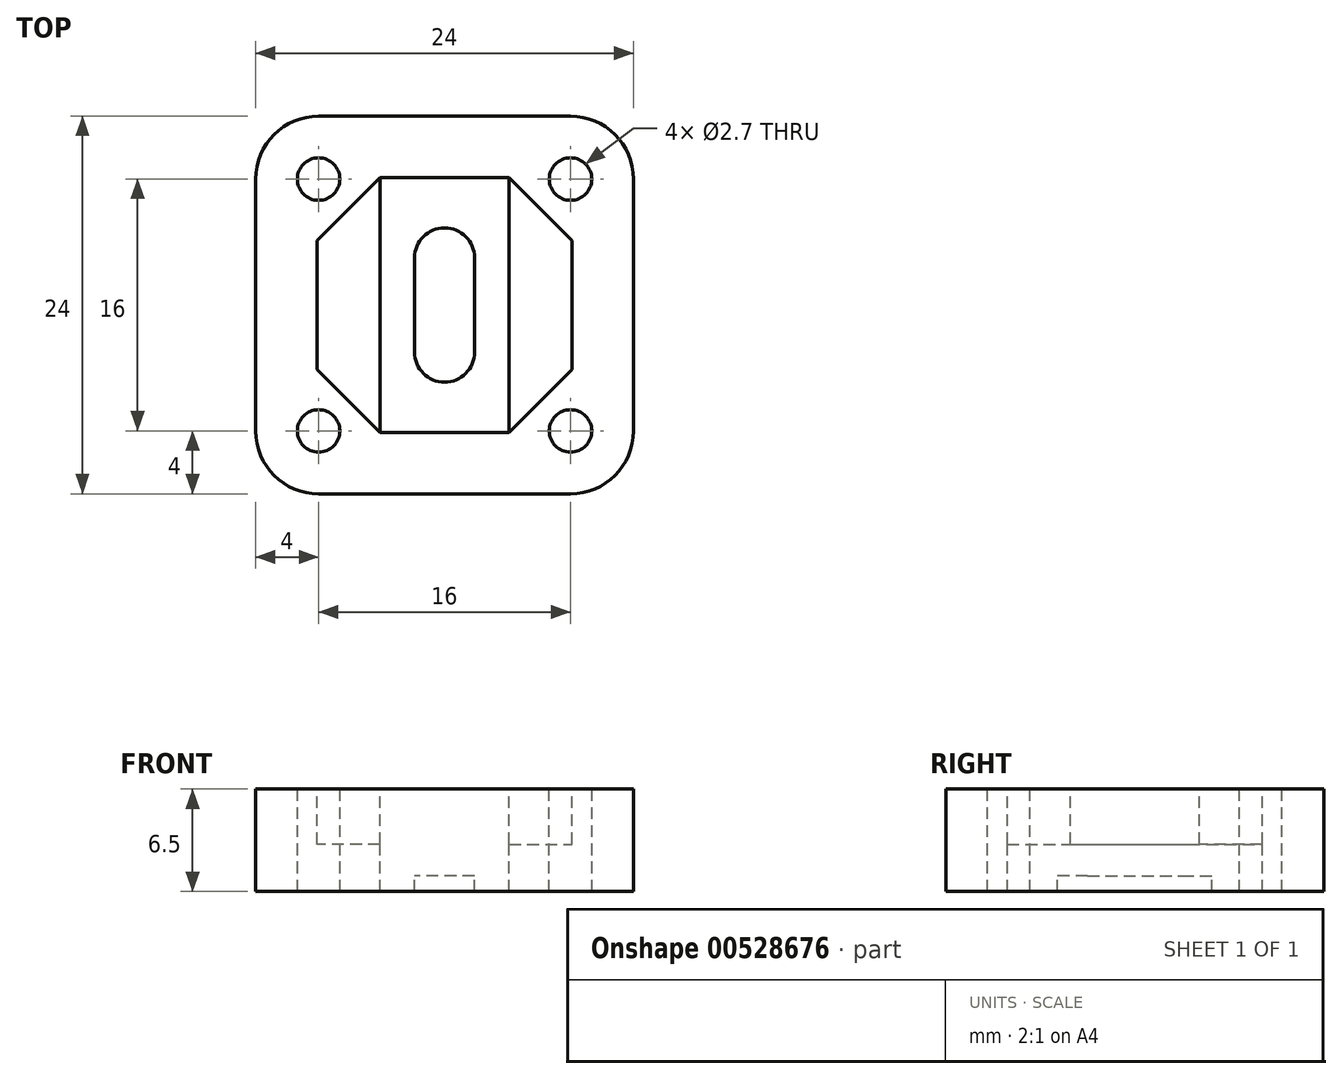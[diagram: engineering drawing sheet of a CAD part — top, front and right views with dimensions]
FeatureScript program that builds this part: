
annotation { "Feature Type Name" : "Feature", "Feature Type Description" : "" }
export const myFeature = defineFeature(function(context is Context, id is Id, definition is map)
    precondition{}
    {
        {
            var Q0;
            Q0=qCreatedBy(makeId("Top.planeOp"),FACE);
            var sketch = newSketch(context, id + "F0", { "sketchPlane" : qUnion([Q0])});
            skLineSegment(sketch, "E0.bottom", {"start": v(0, 0) * mm, "end": v(24, 0) * mm});
            skLineSegment(sketch, "E0.top", {"start": v(0, 24) * mm, "end": v(24, 24) * mm});
            skLineSegment(sketch, "E0.left", {"start": v(0, 0) * mm, "end": v(0, 24) * mm});
            skLineSegment(sketch, "E0.right", {"start": v(24, 0) * mm, "end": v(24, 24) * mm});
            skSolve(sketch);
        }
        {
            var Q0;
            Q0=makeQuery(id+"F0.imprint","IMPRINT",FACE,{"disambiguationData":[TD([[makeQuery(id+"F0.imprint","IMPRINT",EDGE,{"derivedFrom":sQuery(id+"F0.wireOp",EDGE,"E0.bottom")}),1.0]])]});
            extrude(context, id + "F1", {"entities" : qUnion([Q0]), "depth" : 6.5 * mm, "offsetDistance" : 25 * mm});
        }
        {
            var Q0;
            Q0=qCreatedBy(makeId("Top.planeOp"),FACE);
            cPlane(context, id + "F2", {"entities" : qUnion([Q0]), "cplaneType" : CPlaneType.OFFSET, "offset" : 1 * mm, "width" : 150 * mm, "height" : 150 * mm});
        }
        {
            var Q0;
            Q0=qCreatedBy(makeId("Top.planeOp"),FACE);
            cPlane(context, id + "F3", {"entities" : qUnion([Q0]), "cplaneType" : CPlaneType.OFFSET, "offset" : 3 * mm, "width" : 150 * mm, "height" : 150 * mm});
        }
        {
            var Q0;
            Q0=makeQuery(id+"F1.opExtrude","SWEPT_EDGE",EDGE,{"disambiguationData":[OSD([sQuery(id+"F0.wireOp",EDGE,"E0.bottom"),sQuery(id+"F0.wireOp",EDGE,"E0.left")])]});
            var Q1;
            Q1=makeQuery(id+"F1.opExtrude","SWEPT_EDGE",EDGE,{"disambiguationData":[OSD([sQuery(id+"F0.wireOp",EDGE,"E0.bottom"),sQuery(id+"F0.wireOp",EDGE,"E0.right")])]});
            var Q2;
            Q2=makeQuery(id+"F1.opExtrude","SWEPT_EDGE",EDGE,{"disambiguationData":[OSD([sQuery(id+"F0.wireOp",EDGE,"E0.top"),sQuery(id+"F0.wireOp",EDGE,"E0.right")])]});
            var Q3;
            Q3=makeQuery(id+"F1.opExtrude","SWEPT_EDGE",EDGE,{"disambiguationData":[OSD([sQuery(id+"F0.wireOp",EDGE,"E0.top"),sQuery(id+"F0.wireOp",EDGE,"E0.left")])]});
            fillet(context, id + "F4", {"entities" : qUnion([Q0, Q1, Q2, Q3]), "radius" : 4 * mm, "tangentPropagation" : true, "allowEdgeOverflow" : false});
        }
        {
            var Q0;
            Q0=makeQuery(id+"F1.opExtrude","CAP_FACE",FACE,{"disambiguationData":[OSD([sQuery(id+"F0.wireOp",EDGE,"E0.bottom"),sQuery(id+"F0.wireOp",EDGE,"E0.top"),sQuery(id+"F0.wireOp",EDGE,"E0.left"),sQuery(id+"F0.wireOp",EDGE,"E0.right")])],"isStart":false});
            var sketch = newSketch(context, id + "F5", { "sketchPlane" : qUnion([Q0])});
            skCircle(sketch, "E1", {"center": v(4, 4) * mm, "radius": 1.35 * mm});
            skCircle(sketch, "E2.0.1.0", {"center": v(4, 20) * mm, "radius": 1.35 * mm});
            skCircle(sketch, "E2.1.0.0", {"center": v(20, 4) * mm, "radius": 1.35 * mm});
            skCircle(sketch, "E2.1.1.0", {"center": v(20, 20) * mm, "radius": 1.35 * mm});
            skLineSegment(sketch, "E2.direction1", {"start": v(4, 4) * mm, "end": v(20, 4) * mm, "construction": true});
            skLineSegment(sketch, "E2.direction2", {"start": v(4, 4) * mm, "end": v(4, 20) * mm, "construction": true});
            skSolve(sketch);
        }
        {
            var Q0;
            Q0=qSketchRegion(id+"F5",true);
            extrude(context, id + "F6", {"entities" : qUnion([Q0]), "operationType" : NewBodyOperationType.REMOVE, "endBound" : BoundingType.THROUGH_ALL, "oppositeDirection" : true, "depth" : 12 * mm, "offsetDistance" : 25 * mm});
        }
        {
            var Q0;
            Q0=makeQuery(id+"F5.imprint","IMPRINT",FACE,{"disambiguationData":[TD([[makeQuery(id+"F5.imprint","IMPRINT",EDGE,{"derivedFrom":sQuery(id+"F5.wireOp",EDGE,"E1")}),-1.0]])]});
            var sketch = newSketch(context, id + "F7", { "sketchPlane" : qUnion([Q0])});
            skLineSegment(sketch, "E3", {"start": v(12, 12) * mm, "end": v(12, 15) * mm, "construction": true});
            skArc(sketch, "E4", {"start": v(10.1, 15) * mm, "mid": v(12, 16.9) * mm, "end": v(13.9, 15) * mm});
            skLineSegment(sketch, "E5", {"start": v(12, 12) * mm, "end": v(12, 9) * mm, "construction": true});
            skArc(sketch, "E6", {"start": v(10.1, 9) * mm, "mid": v(12, 7.1) * mm, "end": v(13.9, 9) * mm});
            skLineSegment(sketch, "E7", {"start": v(10.1, 15) * mm, "end": v(10.1, 9) * mm});
            skLineSegment(sketch, "E8", {"start": v(13.9, 15) * mm, "end": v(13.9, 9) * mm});
            skLineSegment(sketch, "E9", {"start": v(12, 12) * mm, "end": v(16.1, 12) * mm, "construction": true});
            skLineSegment(sketch, "E10", {"start": v(16.1, 12) * mm, "end": v(16.1, 20.1) * mm});
            skLineSegment(sketch, "E11.MirrorCS", {"start": v(16.1, 12) * mm, "end": v(16.1, 3.9) * mm});
            skLineSegment(sketch, "E12.MirrorCS", {"start": v(7.9, 12) * mm, "end": v(7.9, 20.1) * mm});
            skLineSegment(sketch, "E13.MirrorCS", {"start": v(7.9, 12) * mm, "end": v(7.9, 3.9) * mm});
            skLineSegment(sketch, "E14", {"start": v(16.1, 20.1) * mm, "end": v(7.9, 20.1) * mm});
            skLineSegment(sketch, "E15", {"start": v(16.1, 3.9) * mm, "end": v(7.9, 3.9) * mm});
            skLineSegment(sketch, "E16", {"start": v(12, 12) * mm, "end": v(20.1, 12) * mm, "construction": true});
            skLineSegment(sketch, "E17", {"start": v(20.1, 12) * mm, "end": v(20.1, 16.1) * mm});
            skLineSegment(sketch, "E18", {"start": v(20.1, 16.1) * mm, "end": v(16.1, 20.1) * mm});
            skLineSegment(sketch, "E19.MirrorCS", {"start": v(3.9, 12) * mm, "end": v(3.9, 16.1) * mm});
            skLineSegment(sketch, "E20.MirrorCS", {"start": v(3.9, 16.1) * mm, "end": v(7.9, 20.1) * mm});
            skLineSegment(sketch, "E21.MirrorCS", {"start": v(3.9, 12) * mm, "end": v(3.9, 7.9) * mm});
            skLineSegment(sketch, "E22.MirrorCS", {"start": v(3.9, 7.9) * mm, "end": v(7.9, 3.9) * mm});
            skLineSegment(sketch, "E23.MirrorCS", {"start": v(20.1, 7.9) * mm, "end": v(16.1, 3.9) * mm});
            skLineSegment(sketch, "E24.MirrorCS", {"start": v(20.1, 12) * mm, "end": v(20.1, 7.9) * mm});
            skSolve(sketch);
        }
        {
            var Q0;
            Q0=makeQuery(id+"F7.imprint","IMPRINT",FACE,{"disambiguationData":[TD([[makeQuery(id+"F7.imprint","IMPRINT",EDGE,{"derivedFrom":sQuery(id+"F7.wireOp",EDGE,"E4")}),1.0]])]});
            var Q1;
            Q1=qCreatedBy(id+"F2.planeOp",FACE);
            extrude(context, id + "F8", {"entities" : qUnion([Q0]), "operationType" : NewBodyOperationType.REMOVE, "endBound" : BoundingType.UP_TO_SURFACE, "oppositeDirection" : true, "depth" : 25 * mm, "endBoundEntityFace" : qUnion([Q1]), "offsetDistance" : 25 * mm});
        }
        {
            var Q0;
            Q0=makeQuery(id+"F7.imprint","IMPRINT",FACE,{"disambiguationData":[TD([[makeQuery(id+"F7.imprint","IMPRINT",EDGE,{"derivedFrom":sQuery(id+"F7.wireOp",EDGE,"E4")}),-1.0]])]});
            extrude(context, id + "F9", {"entities" : qUnion([Q0]), "operationType" : NewBodyOperationType.REMOVE, "endBound" : BoundingType.THROUGH_ALL, "oppositeDirection" : true, "depth" : 25 * mm, "offsetDistance" : 25 * mm});
        }
        {
            var Q0;
            Q0=makeQuery(id+"F7.imprint","IMPRINT",FACE,{"disambiguationData":[TD([[makeQuery(id+"F7.imprint","IMPRINT",EDGE,{"derivedFrom":sQuery(id+"F7.wireOp",EDGE,"E12.MirrorCS")}),1.0]])]});
            var Q1;
            Q1=makeQuery(id+"F7.imprint","IMPRINT",FACE,{"disambiguationData":[TD([[makeQuery(id+"F7.imprint","IMPRINT",EDGE,{"derivedFrom":sQuery(id+"F7.wireOp",EDGE,"E10")}),-1.0]])]});
            var Q2;
            Q2=qCreatedBy(id+"F3.planeOp",FACE);
            extrude(context, id + "F10", {"entities" : qUnion([Q0, Q1]), "operationType" : NewBodyOperationType.REMOVE, "endBound" : BoundingType.UP_TO_SURFACE, "oppositeDirection" : true, "depth" : 25 * mm, "endBoundEntityFace" : qUnion([Q2]), "offsetDistance" : 25 * mm});
        }
    });
